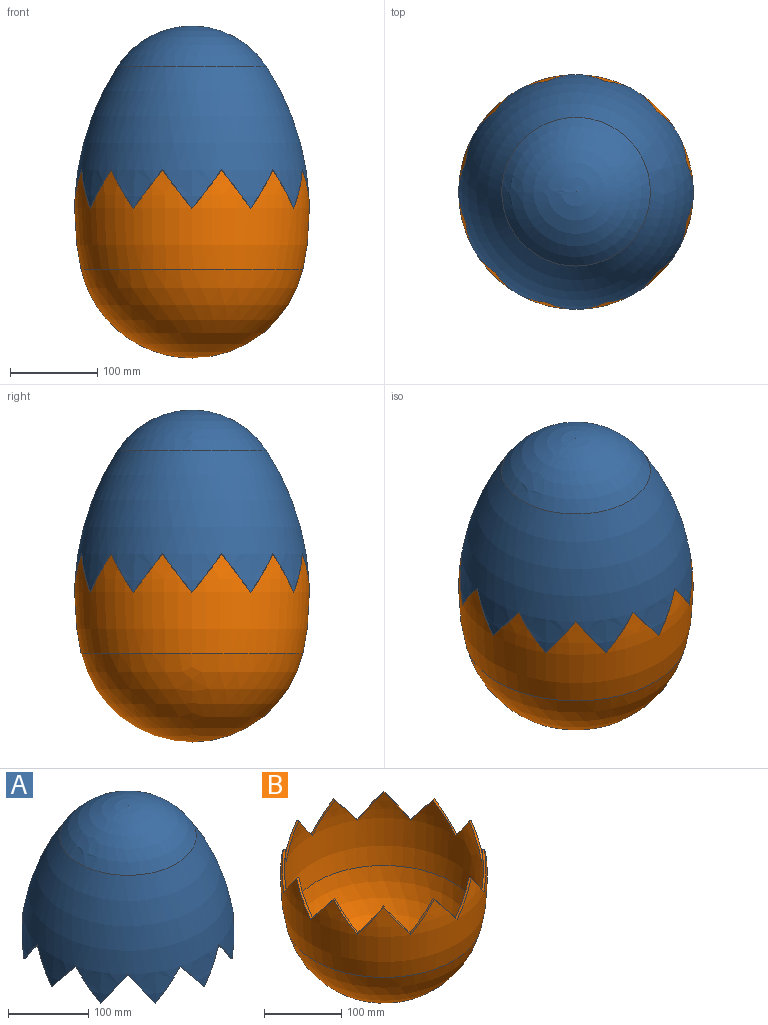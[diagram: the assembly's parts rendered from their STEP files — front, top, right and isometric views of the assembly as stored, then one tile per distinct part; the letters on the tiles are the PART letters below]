
ASSEMBLY  parts=2 mates=1
PART A: 28 faces, bbox 268.9x268.9x209.6 mm
  f0: revolved ~266.63x266.63mm, area 199478.5mm2, adj f1,f2,f3,f6,f7,f8,f9,f10
  f1: sphere r=101.6mm, area 29485.6mm2, adj f0
  f2: plane 44.45x34.22mm, normal (0.2,-0.76,-0.62), area 180mm2, adj f0,f3,f5,f7
  f3: plane 44.45x33.85mm, normal (-0.2,0.76,-0.62), area 180mm2, adj f0,f2,f5,f26
  f4: sphere r=98.42mm, area 27671.6mm2, adj f5
  f5: revolved ~260.31x260.31mm, area 191212.9mm2, adj f2,f3,f4,f6,f7,f8,f9,f10
  f6: plane 44.45x26.86mm, normal (0.56,-0.56,-0.62), area 180mm2, adj f0,f5,f7,f9
  f7: plane 44.45x26.84mm, normal (-0.56,0.56,-0.62), area 180mm2, adj f0,f2,f5,f6
  f8: plane 44.45x33.87mm, normal (0.76,-0.2,-0.62), area 180mm2, adj f0,f5,f9,f11
  f9: plane 44.45x34.22mm, normal (-0.76,0.2,-0.62), area 180mm2, adj f0,f5,f6,f8
  f10: plane 44.45x34.22mm, normal (0.76,0.2,-0.62), area 180mm2, adj f0,f5,f11,f13
  f11: plane 44.45x33.85mm, normal (-0.76,-0.2,-0.62), area 180mm2, adj f0,f5,f8,f10
  f12: plane 44.45x26.86mm, normal (0.56,0.56,-0.62), area 180mm2, adj f0,f5,f13,f15
  f13: plane 44.45x26.84mm, normal (-0.56,-0.56,-0.62), area 180mm2, adj f0,f5,f10,f12
  f14: plane 44.45x33.87mm, normal (0.2,0.76,-0.62), area 180mm2, adj f0,f5,f15,f17
  f15: plane 44.45x34.22mm, normal (-0.2,-0.76,-0.62), area 180mm2, adj f0,f5,f12,f14
  f16: plane 44.45x34.22mm, normal (-0.2,0.76,-0.62), area 180mm2, adj f0,f5,f17,f19
  f17: plane 44.45x33.85mm, normal (0.2,-0.76,-0.62), area 180mm2, adj f0,f5,f14,f16
  f18: plane 44.45x26.86mm, normal (-0.56,0.56,-0.62), area 180mm2, adj f0,f5,f19,f21
  f19: plane 44.45x26.84mm, normal (0.56,-0.56,-0.62), area 180mm2, adj f0,f5,f16,f18
  f20: plane 44.45x33.87mm, normal (-0.76,0.2,-0.62), area 180mm2, adj f0,f5,f21,f23
  f21: plane 44.45x34.22mm, normal (0.76,-0.2,-0.62), area 180mm2, adj f0,f5,f18,f20
  f22: plane 44.45x34.22mm, normal (-0.76,-0.2,-0.62), area 180mm2, adj f0,f5,f23,f25
  f23: plane 44.45x33.85mm, normal (0.76,0.2,-0.62), area 180mm2, adj f0,f5,f20,f22
  f24: plane 44.45x26.86mm, normal (-0.56,-0.56,-0.62), area 180mm2, adj f0,f5,f25,f27
  f25: plane 44.45x26.84mm, normal (0.56,0.56,-0.62), area 180mm2, adj f0,f5,f22,f24
  f26: plane 44.45x33.87mm, normal (-0.2,-0.76,-0.62), area 180mm2, adj f0,f3,f5,f27
  f27: plane 44.45x34.22mm, normal (0.2,0.76,-0.62), area 180mm2, adj f0,f5,f24,f26
PART B: 28 faces, bbox 268.9x268.9x215.9 mm
  f0: sphere r=130.21mm, area 83124.6mm2, adj f1
  f1: revolved ~266.66x266.66mm, area 172928.2mm2, adj f0,f2,f3,f6,f7,f8,f9,f10
  f2: plane 44.45x34.22mm, normal (-0.2,0.76,0.62), area 180mm2, adj f1,f3,f5,f7
  f3: plane 44.45x33.85mm, normal (0.2,-0.76,0.62), area 180mm2, adj f1,f2,f5,f26
  f4: sphere r=127.04mm, area 79120.4mm2, adj f5
  f5: revolved ~260.36x260.36mm, area 168106.7mm2, adj f2,f3,f4,f6,f7,f8,f9,f10
  f6: plane 44.45x26.86mm, normal (-0.56,0.56,0.62), area 180mm2, adj f1,f5,f7,f9
  f7: plane 44.45x26.84mm, normal (0.56,-0.56,0.62), area 180mm2, adj f1,f2,f5,f6
  f8: plane 44.45x33.87mm, normal (-0.76,0.2,0.62), area 180mm2, adj f1,f5,f9,f11
  f9: plane 44.45x34.22mm, normal (0.76,-0.2,0.62), area 180mm2, adj f1,f5,f6,f8
  f10: plane 44.45x34.22mm, normal (-0.76,-0.2,0.62), area 180mm2, adj f1,f5,f11,f13
  f11: plane 44.45x33.85mm, normal (0.76,0.2,0.62), area 180mm2, adj f1,f5,f8,f10
  f12: plane 44.45x26.86mm, normal (-0.56,-0.56,0.62), area 180mm2, adj f1,f5,f13,f15
  f13: plane 44.45x26.84mm, normal (0.56,0.56,0.62), area 180mm2, adj f1,f5,f10,f12
  f14: plane 44.45x33.87mm, normal (-0.2,-0.76,0.62), area 180mm2, adj f1,f5,f15,f17
  f15: plane 44.45x34.22mm, normal (0.2,0.76,0.62), area 180mm2, adj f1,f5,f12,f14
  f16: plane 44.45x34.22mm, normal (0.2,-0.76,0.62), area 180mm2, adj f1,f5,f17,f19
  f17: plane 44.45x33.85mm, normal (-0.2,0.76,0.62), area 180mm2, adj f1,f5,f14,f16
  f18: plane 44.45x26.86mm, normal (0.56,-0.56,0.62), area 180mm2, adj f1,f5,f19,f21
  f19: plane 44.45x26.84mm, normal (-0.56,0.56,0.62), area 180mm2, adj f1,f5,f16,f18
  f20: plane 44.45x33.87mm, normal (0.76,-0.2,0.62), area 180mm2, adj f1,f5,f21,f23
  f21: plane 44.45x34.22mm, normal (-0.76,0.2,0.62), area 180mm2, adj f1,f5,f18,f20
  f22: plane 44.45x34.22mm, normal (0.76,0.2,0.62), area 180mm2, adj f1,f5,f23,f25
  f23: plane 44.45x33.85mm, normal (-0.76,-0.2,0.62), area 180mm2, adj f1,f5,f20,f22
  f24: plane 44.45x26.86mm, normal (0.56,0.56,0.62), area 180mm2, adj f1,f5,f25,f27
  f25: plane 44.45x26.84mm, normal (-0.56,-0.56,0.62), area 180mm2, adj f1,f5,f22,f24
  f26: plane 44.45x33.87mm, normal (0.2,0.76,0.62), area 180mm2, adj f1,f3,f5,f27
  f27: plane 44.45x34.22mm, normal (-0.2,-0.76,0.62), area 180mm2, adj f1,f5,f24,f26
PLACE A t=(0,0,-0.57)mm
PLACE B at identity fixed
MATE slider B.f0 <-> A.f4  axis (0,0,1) through (0,0,130.21)mm
